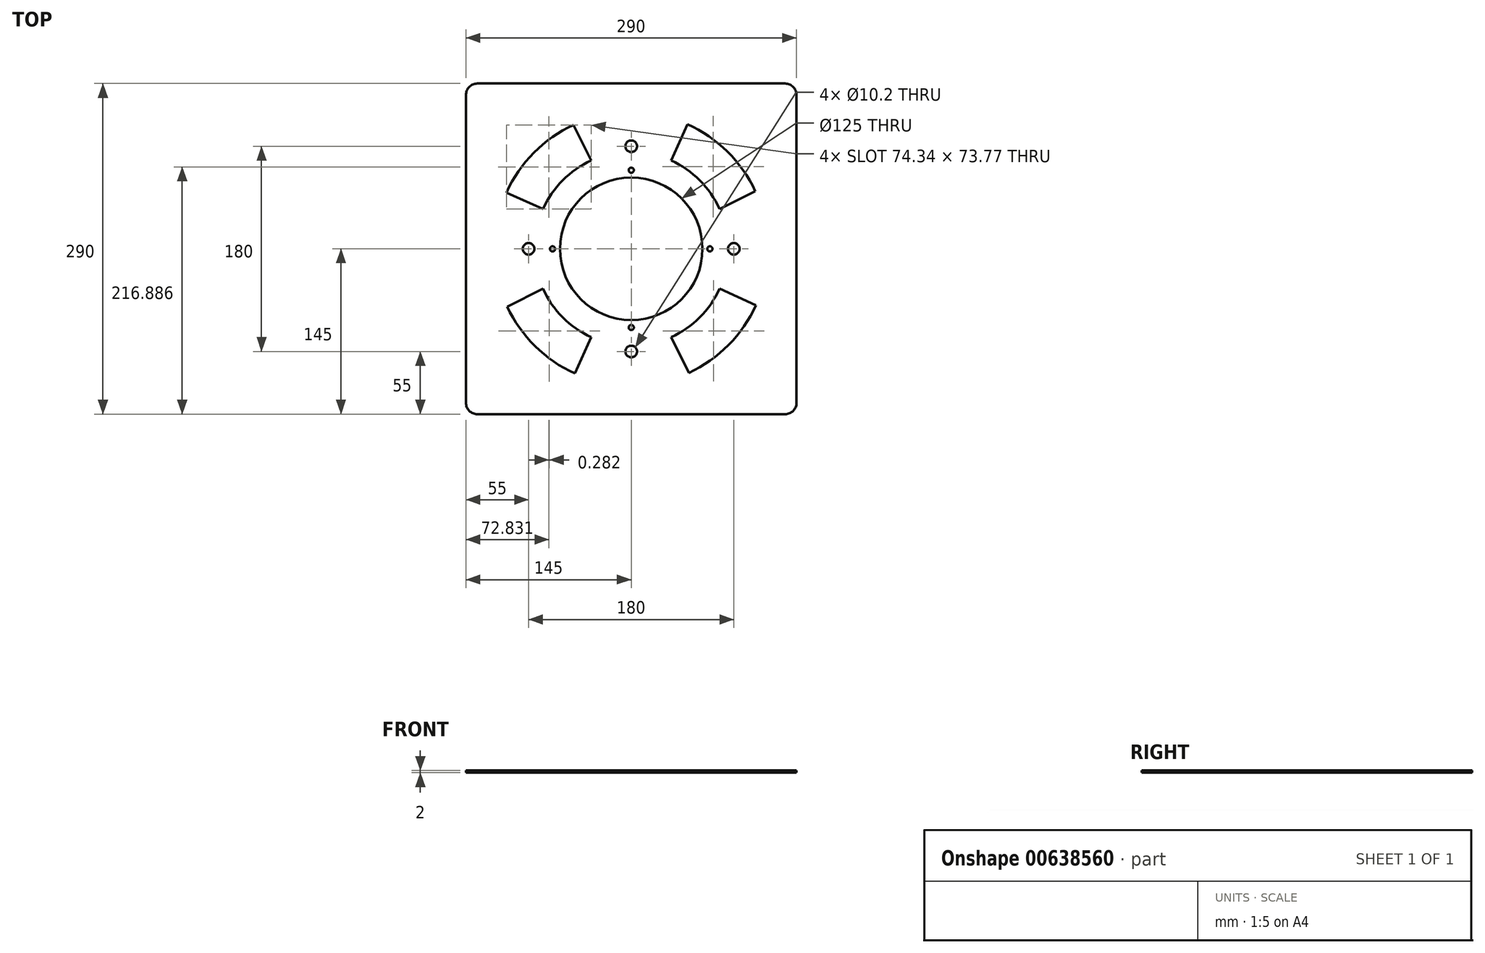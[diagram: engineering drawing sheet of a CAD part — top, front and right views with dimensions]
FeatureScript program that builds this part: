
annotation { "Feature Type Name" : "Feature", "Feature Type Description" : "" }
export const myFeature = defineFeature(function(context is Context, id is Id, definition is map)
    precondition{}
    {
        {
            var Q0;
            Q0=qCreatedBy(makeId("Top.planeOp"),FACE);
            var sketch = newSketch(context, id + "F0", { "sketchPlane" : qUnion([Q0])});
            skLineSegment(sketch, "E0.bottom", {"start": v(-135, 145) * mm, "end": v(135, 145) * mm});
            skLineSegment(sketch, "E0.top", {"start": v(-135, -145) * mm, "end": v(135, -145) * mm});
            skLineSegment(sketch, "E0.left", {"start": v(-145, 135) * mm, "end": v(-145, -135) * mm});
            skLineSegment(sketch, "E0.right", {"start": v(145, 135) * mm, "end": v(145, -135) * mm});
            skPoint(sketch, "E0.middle", {"position": v(0, 0) * mm});
            skCircle(sketch, "E1", {"center": v(0, 0) * mm, "radius": 62.5 * mm});
            skCircle(sketch, "E2", {"center": v(0, 0) * mm, "radius": 69 * mm, "construction": true});
            skCircle(sketch, "E3", {"center": v(0, 69) * mm, "radius": 2.25 * mm});
            skCircle(sketch, "E4.1.0", {"center": v(-69, 0) * mm, "radius": 2.25 * mm});
            skCircle(sketch, "E4.2.0", {"center": v(0, -69) * mm, "radius": 2.25 * mm});
            skCircle(sketch, "E4.3.0", {"center": v(69, 0) * mm, "radius": 2.25 * mm});
            skPoint(sketch, "E5.visualSharp", {"position": v(-145, 145) * mm});
            skArc(sketch, "E5.filletArc", {"start": v(-135, 145) * mm, "mid": v(-142.07, 142.07) * mm, "end": v(-145, 135) * mm});
            skPoint(sketch, "E6.visualSharp", {"position": v(-145, -145) * mm});
            skArc(sketch, "E6.filletArc", {"start": v(-145, -135) * mm, "mid": v(-142.07, -142.07) * mm, "end": v(-135, -145) * mm});
            skPoint(sketch, "E7.visualSharp", {"position": v(145, -145) * mm});
            skArc(sketch, "E7.filletArc", {"start": v(135, -145) * mm, "mid": v(142.07, -142.07) * mm, "end": v(145, -135) * mm});
            skPoint(sketch, "E8.visualSharp", {"position": v(145, 145) * mm});
            skArc(sketch, "E8.filletArc", {"start": v(145, 135) * mm, "mid": v(142.07, 142.07) * mm, "end": v(135, 145) * mm});
            skSolve(sketch);
        }
        {
            var Q0;
            Q0 = qSketchRegion(id + "F0", true);
            extrude(context, id + "F1", {"entities" : qUnion([Q0]), "depth" : 2 * mm, "offsetDistance" : 25 * mm});
        }
        {
            var Q0;
            Q0=makeQuery(id+"F1.opExtrude","CAP_FACE",FACE,{"disambiguationData":[OSD([sQuery(id+"F0.wireOp",EDGE,"E0.bottom"),sQuery(id+"F0.wireOp",EDGE,"E0.top"),sQuery(id+"F0.wireOp",EDGE,"E0.left"),sQuery(id+"F0.wireOp",EDGE,"E0.right"),sQuery(id+"F0.wireOp",EDGE,"E1"),sQuery(id+"F0.wireOp",EDGE,"E3"),sQuery(id+"F0.wireOp",EDGE,"E4.1.0"),sQuery(id+"F0.wireOp",EDGE,"E4.2.0"),sQuery(id+"F0.wireOp",EDGE,"E4.3.0"),sQuery(id+"F0.wireOp",EDGE,"E5.filletArc"),sQuery(id+"F0.wireOp",EDGE,"E6.filletArc"),sQuery(id+"F0.wireOp",EDGE,"E7.filletArc"),sQuery(id+"F0.wireOp",EDGE,"E8.filletArc")])],"isStart":false});
            var sketch = newSketch(context, id + "F2", { "sketchPlane" : qUnion([Q0])});
            skCircle(sketch, "E9", {"center": v(0, 0) * mm, "radius": 90 * mm, "construction": true});
            skCircle(sketch, "E10", {"center": v(0, 90) * mm, "radius": 5.1 * mm});
            skCircle(sketch, "E11.1.0", {"center": v(-90, 0) * mm, "radius": 5.1 * mm});
            skCircle(sketch, "E11.2.0", {"center": v(0, -90) * mm, "radius": 5.1 * mm});
            skCircle(sketch, "E11.3.0", {"center": v(90, 0) * mm, "radius": 5.1 * mm});
            skSolve(sketch);
        }
        {
            var Q0;
            Q0 = qSketchRegion(id + "F2", true);
            extrude(context, id + "F3", {"entities" : qUnion([Q0]), "operationType" : NewBodyOperationType.REMOVE, "oppositeDirection" : true, "depth" : 25 * mm, "offsetDistance" : 25 * mm});
        }
        {
            var Q0;
            Q0=makeQuery(id+"F1.opExtrude","CAP_FACE",FACE,{"disambiguationData":[OSD([sQuery(id+"F0.wireOp",EDGE,"E0.bottom"),sQuery(id+"F0.wireOp",EDGE,"E0.top"),sQuery(id+"F0.wireOp",EDGE,"E0.left"),sQuery(id+"F0.wireOp",EDGE,"E0.right"),sQuery(id+"F0.wireOp",EDGE,"E1"),sQuery(id+"F0.wireOp",EDGE,"E3"),sQuery(id+"F0.wireOp",EDGE,"E4.1.0"),sQuery(id+"F0.wireOp",EDGE,"E4.2.0"),sQuery(id+"F0.wireOp",EDGE,"E4.3.0"),sQuery(id+"F0.wireOp",EDGE,"E5.filletArc"),sQuery(id+"F0.wireOp",EDGE,"E6.filletArc"),sQuery(id+"F0.wireOp",EDGE,"E7.filletArc"),sQuery(id+"F0.wireOp",EDGE,"E8.filletArc")])],"isStart":false});
            var sketch = newSketch(context, id + "F4", { "sketchPlane" : qUnion([Q0])});
            skCircle(sketch, "E12", {"center": v(0, 0) * mm, "radius": 82.5 * mm, "construction": true});
            skCircle(sketch, "E13", {"center": v(0, 0) * mm, "radius": 120 * mm, "construction": true});
            skCircle(sketch, "E14", {"center": v(0, 0) * mm, "radius": 119.98 * mm});
            skCircle(sketch, "E15", {"center": v(0, 0) * mm, "radius": 85 * mm});
            skLineSegment(sketch, "E16", {"start": v(-35, 77.46) * mm, "end": v(-50.64, 108.77) * mm});
            skLineSegment(sketch, "E17", {"start": v(-77.46, 35) * mm, "end": v(-109.35, 49.41) * mm});
            skLineSegment(sketch, "E18.1.0", {"start": v(-77.46, -35) * mm, "end": v(-108.77, -50.64) * mm});
            skLineSegment(sketch, "E18.1.1", {"start": v(-35, -77.46) * mm, "end": v(-49.41, -109.35) * mm});
            skLineSegment(sketch, "E18.2.0", {"start": v(35, -77.46) * mm, "end": v(50.64, -108.77) * mm});
            skLineSegment(sketch, "E18.2.1", {"start": v(77.46, -35) * mm, "end": v(109.35, -49.41) * mm});
            skLineSegment(sketch, "E18.3.0", {"start": v(77.46, 35) * mm, "end": v(108.77, 50.64) * mm});
            skLineSegment(sketch, "E18.3.1", {"start": v(35, 77.46) * mm, "end": v(49.41, 109.35) * mm});
            skSolve(sketch);
        }
        {
            var Q0;
            {var subQ0=sQuery(id+"F4.wireOp",EDGE,"E16");Q0=makeQuery(id+"F4.imprint","IMPRINT",FACE,{"disambiguationData":[TD([[makeQuery(id+"F4.imprint","IMPRINT",EDGE,{"derivedFrom":subQ0}),1.0]])]});}
            var Q1;
            {var subQ0=sQuery(id+"F4.wireOp",EDGE,"E18.3.0");Q1=makeQuery(id+"F4.imprint","IMPRINT",FACE,{"disambiguationData":[TD([[makeQuery(id+"F4.imprint","IMPRINT",EDGE,{"derivedFrom":subQ0}),1.0]])]});}
            var Q2;
            {var subQ0=sQuery(id+"F4.wireOp",EDGE,"E18.2.0");Q2=makeQuery(id+"F4.imprint","IMPRINT",FACE,{"disambiguationData":[TD([[makeQuery(id+"F4.imprint","IMPRINT",EDGE,{"derivedFrom":subQ0}),1.0]])]});}
            var Q3;
            {var subQ0=sQuery(id+"F4.wireOp",EDGE,"E18.1.0");Q3=makeQuery(id+"F4.imprint","IMPRINT",FACE,{"disambiguationData":[TD([[makeQuery(id+"F4.imprint","IMPRINT",EDGE,{"derivedFrom":subQ0}),1.0]])]});}
            extrude(context, id + "F5", {"entities" : qUnion([Q0, Q1, Q2, Q3]), "operationType" : NewBodyOperationType.REMOVE, "oppositeDirection" : true, "depth" : 25 * mm, "offsetDistance" : 25 * mm});
        }
    });
